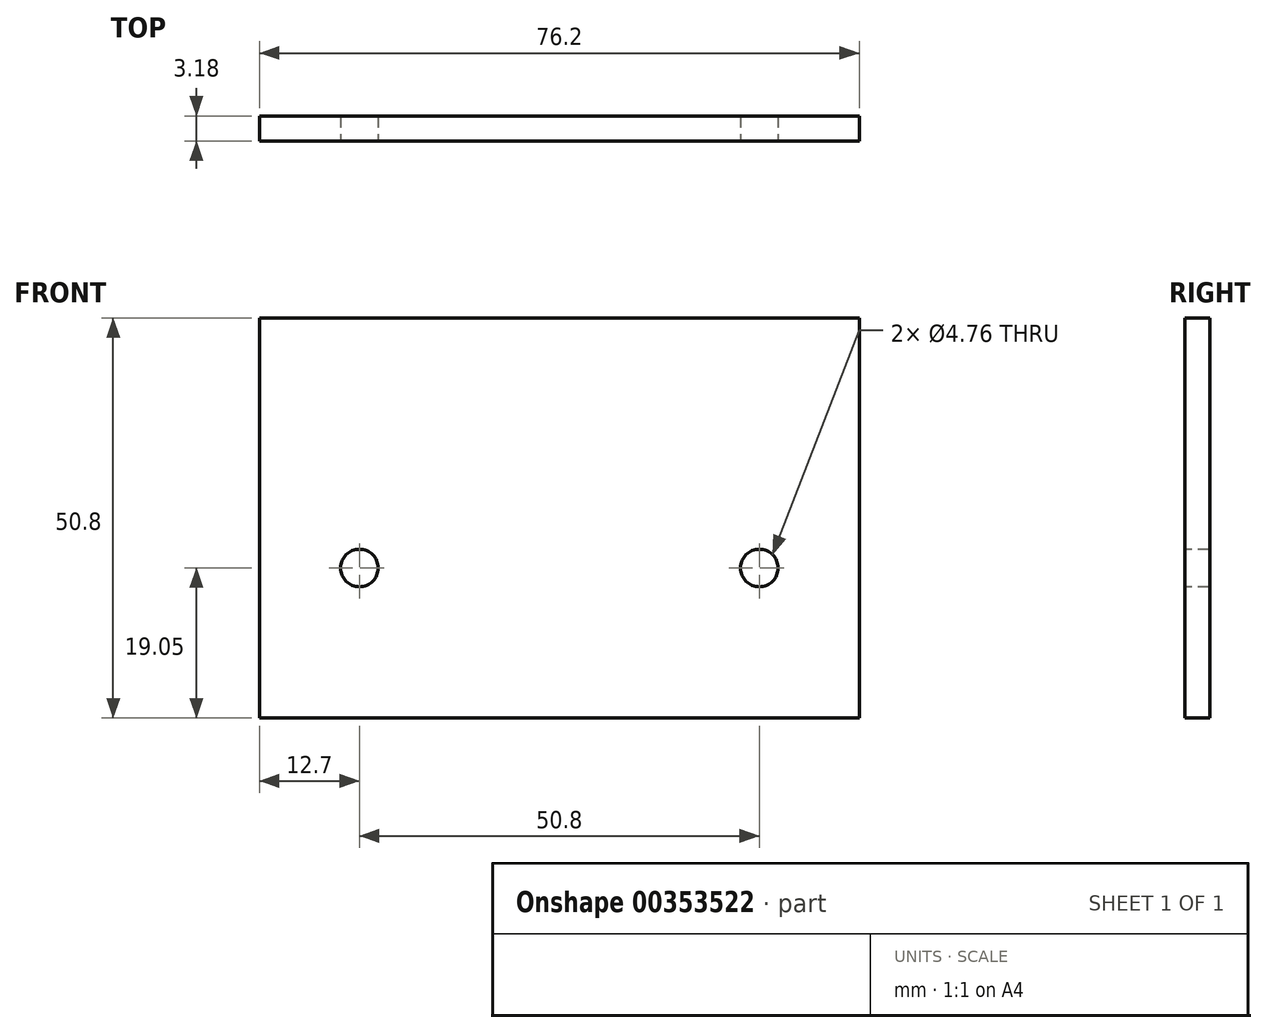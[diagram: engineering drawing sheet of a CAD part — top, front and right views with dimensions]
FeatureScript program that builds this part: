
annotation { "Feature Type Name" : "Feature", "Feature Type Description" : "" }
export const myFeature = defineFeature(function(context is Context, id is Id, definition is map)
    precondition{}
    {
        {
            var Q0;
            Q0=qCreatedBy(makeId("Front.planeOp"),FACE);
            var sketch = newSketch(context, id + "F0", { "sketchPlane" : qUnion([Q0])});
            skLineSegment(sketch, "E0.bottom", {"start": v(38.1, 25.4) * mm, "end": v(-38.1, 25.4) * mm});
            skLineSegment(sketch, "E0.top", {"start": v(38.1, -25.4) * mm, "end": v(-38.1, -25.4) * mm});
            skLineSegment(sketch, "E0.left", {"start": v(38.1, 25.4) * mm, "end": v(38.1, -25.4) * mm});
            skLineSegment(sketch, "E0.right", {"start": v(-38.1, 25.4) * mm, "end": v(-38.1, -25.4) * mm});
            skPoint(sketch, "E0.middle", {"position": v(0, 0) * mm});
            skSolve(sketch);
        }
        {
            var Q0;
            Q0 = qSketchRegion(id + "F0", true);
            extrude(context, id + "F1", {"entities" : qUnion([Q0]), "depth" : 3.17 * mm});
        }
        {
            var Q0;
            Q0=makeQuery(id+"F1.opExtrude","CAP_FACE",FACE,{"disambiguationData":[OSD([sQuery(id+"F0.wireOp",EDGE,"E0.bottom"),sQuery(id+"F0.wireOp",EDGE,"E0.top"),sQuery(id+"F0.wireOp",EDGE,"E0.left"),sQuery(id+"F0.wireOp",EDGE,"E0.right")])],"isStart":false});
            var sketch = newSketch(context, id + "F2", { "sketchPlane" : qUnion([Q0])});
            skPoint(sketch, "E1", {"position": v(-25.4, -6.35) * mm});
            skPoint(sketch, "E2", {"position": v(25.4, -6.35) * mm});
            skCircle(sketch, "E3", {"center": v(-25.4, -6.35) * mm, "radius": 2.38 * mm});
            skCircle(sketch, "E4", {"center": v(25.4, -6.35) * mm, "radius": 2.38 * mm});
            skSolve(sketch);
        }
        {
            var Q0;
            Q0 = qSketchRegion(id + "F2", true);
            extrude(context, id + "F3", {"entities" : qUnion([Q0]), "operationType" : NewBodyOperationType.REMOVE, "oppositeDirection" : true, "depth" : 3.17 * mm});
        }
    });
